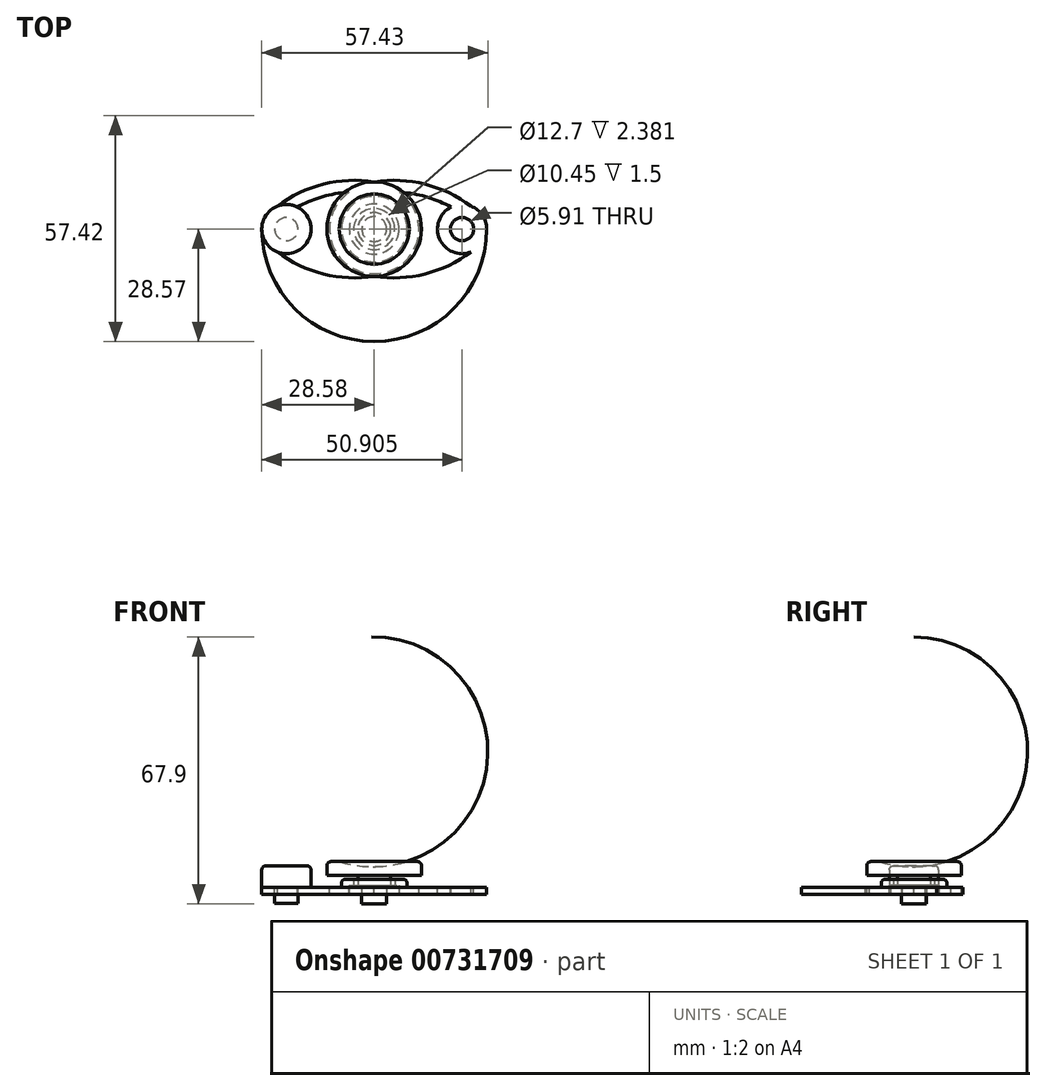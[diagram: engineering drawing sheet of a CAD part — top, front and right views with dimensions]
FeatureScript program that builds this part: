
annotation { "Feature Type Name" : "Feature", "Feature Type Description" : "" }
export const myFeature = defineFeature(function(context is Context, id is Id, definition is map)
    precondition{}
    {
        {
            var Q0;
            Q0=qCreatedBy(makeId("Front.planeOp"),FACE);
            var sketch = newSketch(context, id + "F0", { "sketchPlane" : qUnion([Q0])});
            skLineSegment(sketch, "E0", {"start": v(0, 0) * mm, "end": v(0, 6.26) * mm});
            skLineSegment(sketch, "E1", {"start": v(-6.35, 0) * mm, "end": v(-6.35, 2.38) * mm});
            skLineSegment(sketch, "E2", {"start": v(-6.35, 2.38) * mm, "end": v(-5.23, 2.38) * mm});
            skLineSegment(sketch, "E3", {"start": v(-5.23, 2.38) * mm, "end": v(-5.23, 3.88) * mm});
            skLineSegment(sketch, "E4", {"start": v(-6.35, 0) * mm, "end": v(-8.35, 0) * mm});
            skLineSegment(sketch, "E5", {"start": v(-5.23, 3.88) * mm, "end": v(-8.35, 3.88) * mm});
            skLineSegment(sketch, "E6", {"start": v(-8.35, 3.88) * mm, "end": v(-8.35, 1.8) * mm});
            skLineSegment(sketch, "E7", {"start": v(-8.35, 1.8) * mm, "end": v(-28.58, 1.8) * mm});
            skLineSegment(sketch, "E8", {"start": v(-28.58, 1.8) * mm, "end": v(-28.58, 0) * mm});
            skLineSegment(sketch, "E9", {"start": v(-28.58, 0) * mm, "end": v(-8.35, 0) * mm});
            skLineSegment(sketch, "E10", {"start": v(-3.18, 0) * mm, "end": v(-3.18, -2.38) * mm});
            skLineSegment(sketch, "E11", {"start": v(0, 10.42) * mm, "end": v(-12, 10.42) * mm});
            skLineSegment(sketch, "E12", {"start": v(-4.17, 4.88) * mm, "end": v(-12, 4.88) * mm});
            skPoint(sketch, "E13.end.orphan", {"position": v(-28.58, 6.26) * mm});
            skPoint(sketch, "E14.end.orphan", {"position": v(-3.18, 3.88) * mm});
            skLineSegment(sketch, "E15", {"start": v(-3.18, 0) * mm, "end": v(-3.18, 2.38) * mm});
            skLineSegment(sketch, "E16", {"start": v(-3.18, 2.38) * mm, "end": v(-4.17, 2.38) * mm});
            skLineSegment(sketch, "E17", {"start": v(-4.17, 2.38) * mm, "end": v(-4.17, 4.88) * mm});
            skLineSegment(sketch, "E18", {"start": v(-12, 4.88) * mm, "end": v(-12, 8.38) * mm});
            skLineSegment(sketch, "E19", {"start": v(-12, 8.38) * mm, "end": v(-8.91, 8.38) * mm});
            skLineSegment(sketch, "E20", {"start": v(0, 7.1) * mm, "end": v(0, -2.38) * mm});
            skLineSegment(sketch, "E21", {"start": v(0, -2.38) * mm, "end": v(-3.18, -2.38) * mm});
            skArc(sketch, "E22", {"start": v(-8.91, 8.38) * mm, "mid": v(-4.5, 7.4) * mm, "end": v(0, 7.1) * mm});
            skPoint(sketch, "E23.orphan", {"position": v(0, 8.38) * mm});
            skSolve(sketch);
        }
        {
            var Q0;
            Q0=makeQuery(id+"F0.imprint","IMPRINT",FACE,{"disambiguationData":[TD([[makeQuery(id+"F0.imprint","IMPRINT",EDGE,{"derivedFrom":sQuery(id+"F0.wireOp",EDGE,"E1")}),1.0]])]});
            var Q1;
            Q1=makeQuery(id+"F0.imprint","IMPRINT",FACE,{"disambiguationData":[TD([[makeQuery(id+"F0.imprint","IMPRINT",EDGE,{"derivedFrom":sQuery(id+"F0.wireOp",EDGE,"E10")}),1.0]])]});
            var Q2;
            Q2=sQuery(id+"F0.wireOp",EDGE,"E0");
            revolve(context, id + "F1", {"surfaceOperationType" : NewSurfaceOperationType.NEW, "entities" : qUnion([Q0, Q1]), "axis" : qUnion([Q2]), "revolveType" : RevolveType.FULL});
        }
        {
            var Q0;
            Q0=makeQuery(id+"F1.opRevolve","SWEPT_FACE",FACE,{"disambiguationData":[OSD([sQuery(id+"F0.wireOp",EDGE,"E7")])]});
            var sketch = newSketch(context, id + "F2", { "sketchPlane" : qUnion([Q0])});
            skCircle(sketch, "E24", {"center": v(-22.33, 0) * mm, "radius": 6.25 * mm});
            skArc(sketch, "E25", {"start": v(0, 12) * mm, "mid": v(-12.91, 11.4) * mm, "end": v(-24.57, 5.83) * mm});
            skArc(sketch, "E26.MirrorCS", {"start": v(0, -12) * mm, "mid": v(-12.91, -11.4) * mm, "end": v(-24.57, -5.83) * mm});
            skCircle(sketch, "E27.0", {"center": v(0, 0) * mm, "radius": 11.35 * mm});
            skArc(sketch, "E28.0", {"start": v(-0.46, -9.04) * mm, "mid": v(-12.18, -8.5) * mm, "end": v(-22.77, -3.43) * mm});
            skArc(sketch, "E29.0", {"start": v(-0.46, 9.04) * mm, "mid": v(-12.18, 8.5) * mm, "end": v(-22.77, 3.43) * mm});
            skPoint(sketch, "E30.start.orphan", {"position": v(-12, 0) * mm});
            skLineSegment(sketch, "E31", {"start": v(0, 2.89) * mm, "end": v(0, -2.96) * mm});
            skArc(sketch, "E32.MirrorCS", {"start": v(0.46, -9.04) * mm, "mid": v(12.18, -8.5) * mm, "end": v(22.77, -3.43) * mm});
            skArc(sketch, "E33.MirrorCS", {"start": v(0, -12) * mm, "mid": v(12.91, -11.4) * mm, "end": v(24.57, -5.83) * mm});
            skArc(sketch, "E34.MirrorCS", {"start": v(0.46, 9.04) * mm, "mid": v(12.18, 8.5) * mm, "end": v(22.77, 3.43) * mm});
            skArc(sketch, "E35.MirrorCS", {"start": v(0, 12) * mm, "mid": v(12.91, 11.4) * mm, "end": v(24.57, 5.83) * mm});
            skCircle(sketch, "E36.MirrorC", {"center": v(22.33, 0) * mm, "radius": 6.25 * mm});
            skCircle(sketch, "E37", {"center": v(22.33, 0) * mm, "radius": 2.96 * mm});
            skCircle(sketch, "E38.MirrorC", {"center": v(-22.33, 0) * mm, "radius": 2.96 * mm});
            skSolve(sketch);
        }
        {
            var Q0;
            {var subQ4=sQuery(id+"F2.wireOp",EDGE,"E26.MirrorCS");Q0=makeQuery(id+"F2.imprint","IMPRINT",FACE,{"disambiguationData":[TD([[makeQuery(id+"F2.imprint","IMPRINT",EDGE,{"derivedFrom":subQ4}),1.0]])]});}
            var Q1;
            Q1=makeQuery(id+"F2.imprint","IMPRINT",FACE,{"disambiguationData":[TD([[makeQuery(id+"F2.imprint","IMPRINT",EDGE,{"derivedFrom":sQuery(id+"F2.wireOp",EDGE,"E37")}),1.0]])]});
            var Q2;
            {var subQ0=sQuery(id+"F2.wireOp",EDGE,"E34.MirrorCS");var subQ1=sQuery(id+"F2.wireOp",EDGE,"E27.0");var subQ2=makeQuery(id+"F2.imprint","INTERSECT",VERTEX,{"derivedFrom":[subQ1,subQ0]});Q2=makeQuery(id+"F2.imprint","IMPRINT",FACE,{"disambiguationData":[TD([[makeQuery(id+"F2.imprint","IMPRINT",EDGE,{"disambiguationData":[TD([[subQ2,1.0]])],"derivedFrom":subQ1}),-1.0]])]});}
            var Q3;
            {var subQ0=sQuery(id+"F2.wireOp",EDGE,"E29.0");var subQ1=sQuery(id+"F2.wireOp",EDGE,"E24");var subQ2=makeQuery(id+"F2.imprint","INTERSECT",VERTEX,{"derivedFrom":[subQ1,subQ0]});Q3=makeQuery(id+"F2.imprint","IMPRINT",FACE,{"disambiguationData":[TD([[makeQuery(id+"F2.imprint","IMPRINT",EDGE,{"disambiguationData":[TD([[subQ2,1.0]])],"derivedFrom":subQ1}),-1.0]])]});}
            var Q4;
            Q4=makeQuery(id+"F2.imprint","IMPRINT",FACE,{"disambiguationData":[TD([[makeQuery(id+"F2.imprint","IMPRINT",EDGE,{"derivedFrom":sQuery(id+"F2.wireOp",EDGE,"E38.MirrorC")}),-1.0]])]});
            var Q5;
            {var subQ4=sQuery(id+"F2.wireOp",EDGE,"E25");Q5=makeQuery(id+"F2.imprint","IMPRINT",FACE,{"disambiguationData":[TD([[makeQuery(id+"F2.imprint","IMPRINT",EDGE,{"derivedFrom":subQ4}),-1.0]])]});}
            extrude(context, id + "F3", {"entities" : qUnion([Q0, Q1, Q2, Q3, Q4, Q5]), "operationType" : NewBodyOperationType.REMOVE, "oppositeDirection" : true, "depth" : 25 * mm, "offsetDistance" : 25 * mm});
        }
        {
            var Q0;
            Q0=makeQuery(id+"F1.opRevolve","SWEPT_EDGE",EDGE,{"disambiguationData":[OSD([sQuery(id+"F0.wireOp",EDGE,"E5"),sQuery(id+"F0.wireOp",EDGE,"E6")])]});
            fillet(context, id + "F4", {"entities" : qUnion([Q0]), "radius" : 1 * mm, "tangentPropagation" : true, "allowEdgeOverflow" : false});
        }
        {
            var Q0;
            Q0=makeQuery(id+"F1.opRevolve","SWEPT_EDGE",EDGE,{"disambiguationData":[OSD([sQuery(id+"F0.wireOp",EDGE,"E18"),sQuery(id+"F0.wireOp",EDGE,"E19")])]});
            fillet(context, id + "F5", {"entities" : qUnion([Q0]), "radius" : 1 * mm, "tangentPropagation" : true, "allowEdgeOverflow" : false});
        }
        {
            var Q0;
            Q0=makeQuery(id+"F2.imprint","IMPRINT",FACE,{"disambiguationData":[TD([[makeQuery(id+"F2.imprint","IMPRINT",EDGE,{"derivedFrom":sQuery(id+"F2.wireOp",EDGE,"E38.MirrorC")}),1.0]])]});
            var Q1;
            Q1=makeQuery(id+"F2.imprint","IMPRINT",FACE,{"disambiguationData":[TD([[makeQuery(id+"F2.imprint","IMPRINT",EDGE,{"derivedFrom":sQuery(id+"F2.wireOp",EDGE,"E38.MirrorC")}),-1.0]])]});
            extrude(context, id + "F6", {"entities" : qUnion([Q0, Q1]), "depth" : 5.5 * mm, "offsetDistance" : 25 * mm});
        }
        {
            var Q0;
            Q0=makeQuery(id+"F6.opExtrude","CAP_EDGE",EDGE,{"disambiguationData":[OSD([sQuery(id+"F2.wireOp",EDGE,"E24")])],"isStart":false});
            fillet(context, id + "F7", {"entities" : qUnion([Q0]), "radius" : 1 * mm, "tangentPropagation" : true, "allowEdgeOverflow" : false});
        }
        {
            var Q0;
            Q0=makeQuery(id+"F6.opExtrude","CAP_FACE",FACE,{"disambiguationData":[OSD([sQuery(id+"F2.wireOp",EDGE,"E24")])],"isStart":true});
            var sketch = newSketch(context, id + "F8", { "sketchPlane" : qUnion([Q0])});
            skCircle(sketch, "E39", {"center": v(-22.33, 0) * mm, "radius": 2.96 * mm});
            skSolve(sketch);
        }
        {
            var Q0;
            Q0 = qSketchRegion(id + "F8", true);
            extrude(context, id + "F9", {"entities" : qUnion([Q0]), "operationType" : NewBodyOperationType.ADD, "depth" : 4 * mm, "offsetDistance" : 25 * mm});
        }
    });
